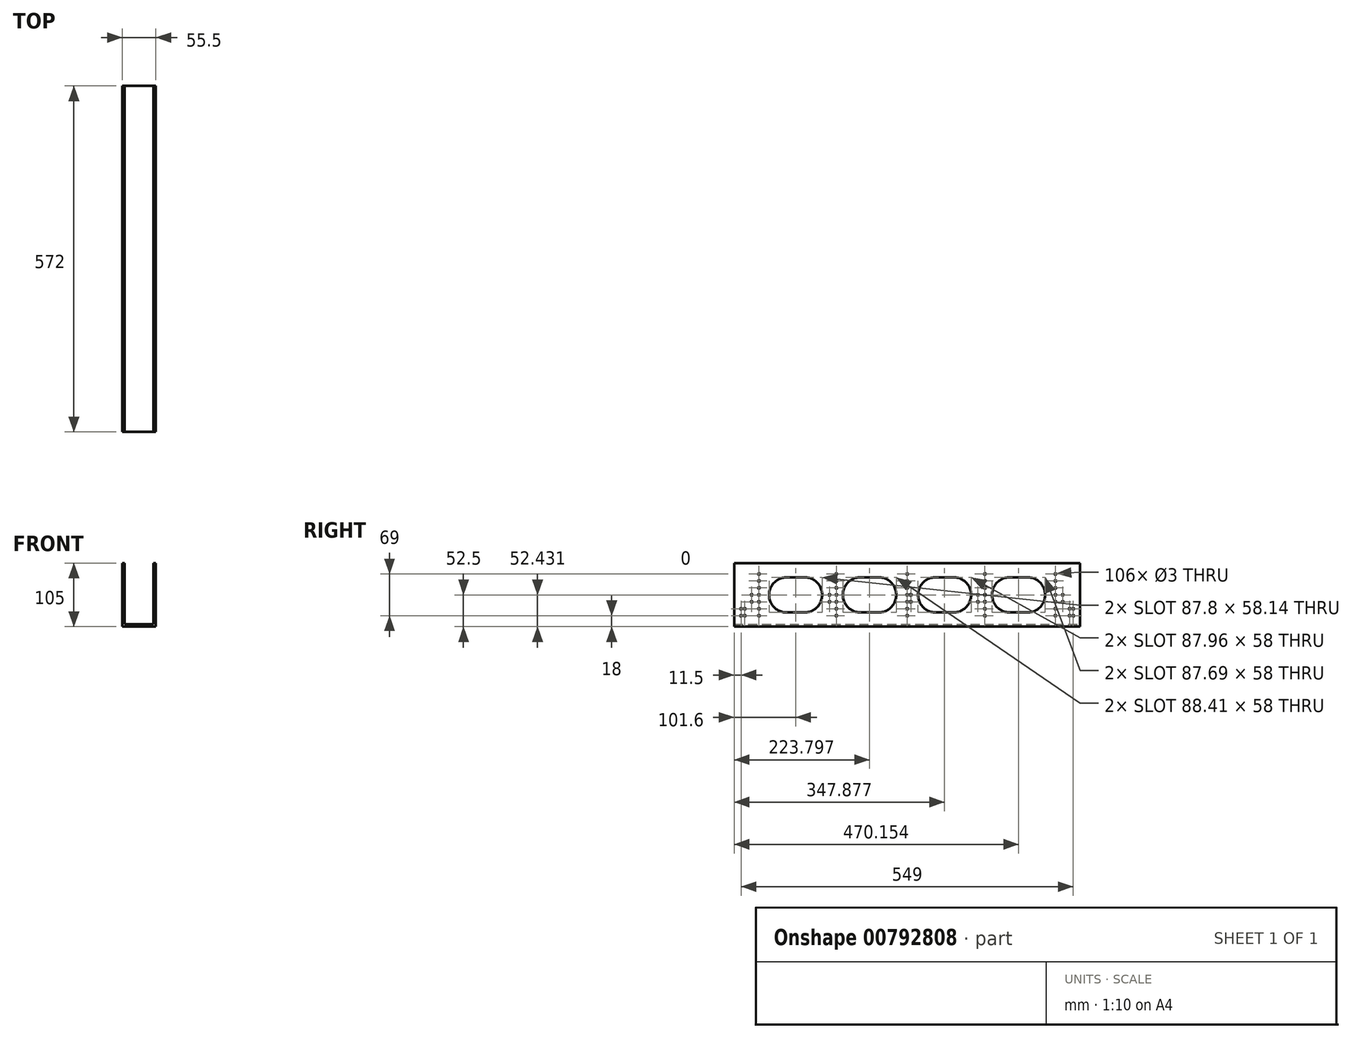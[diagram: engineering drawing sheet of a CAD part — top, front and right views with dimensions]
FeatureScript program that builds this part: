
annotation { "Feature Type Name" : "Feature", "Feature Type Description" : "" }
export const myFeature = defineFeature(function(context is Context, id is Id, definition is map)
    precondition{}
    {
        {
            var Q0;
            Q0=qCreatedBy(makeId("Right.planeOp"),FACE);
            var sketch = newSketch(context, id + "F0", { "sketchPlane" : qUnion([Q0])});
            skLineSegment(sketch, "E0.bottom", {"start": v(286, -52.5) * mm, "end": v(-286, -52.5) * mm});
            skLineSegment(sketch, "E0.top", {"start": v(286, 52.5) * mm, "end": v(-286, 52.5) * mm});
            skLineSegment(sketch, "E0.left", {"start": v(286, -52.5) * mm, "end": v(286, 52.5) * mm});
            skLineSegment(sketch, "E0.right", {"start": v(-286, -52.5) * mm, "end": v(-286, 52.5) * mm});
            skPoint(sketch, "E0.middle", {"position": v(0, 0) * mm});
            skPoint(sketch, "E1.startSnap0", {"position": v(-286, 0) * mm});
            skCircle(sketch, "E2", {"center": v(-199.3, -0.15) * mm, "radius": 29 * mm});
            skLineSegment(sketch, "E3", {"start": v(-369.82, 0) * mm, "end": v(342.23, 0) * mm, "construction": true});
            skLineSegment(sketch, "E4", {"start": v(-286, -127.41) * mm, "end": v(-286, 126.22) * mm, "construction": true});
            skCircle(sketch, "E5", {"center": v(-169.5, 0) * mm, "radius": 29 * mm});
            skCircle(sketch, "E6", {"center": v(-77.4, 0) * mm, "radius": 29 * mm});
            skCircle(sketch, "E7", {"center": v(-47, 0) * mm, "radius": 29 * mm});
            skCircle(sketch, "E8", {"center": v(46.9, 0) * mm, "radius": 29 * mm});
            skCircle(sketch, "E9", {"center": v(76.86, 0) * mm, "radius": 29 * mm});
            skCircle(sketch, "E10", {"center": v(199, 0) * mm, "radius": 29 * mm});
            skCircle(sketch, "E11", {"center": v(169.3, 0) * mm, "radius": 29 * mm});
            skLineSegment(sketch, "E12", {"start": v(-198.35, 28.83) * mm, "end": v(-169.67, 29) * mm});
            skLineSegment(sketch, "E13", {"start": v(-47.17, 29) * mm, "end": v(-77.4, 29) * mm});
            skLineSegment(sketch, "E14", {"start": v(46.72, 29) * mm, "end": v(76.86, 29) * mm});
            skLineSegment(sketch, "E15", {"start": v(198.83, 29) * mm, "end": v(169.3, 29) * mm});
            skLineSegment(sketch, "E16.MirrorCS", {"start": v(-47.17, -29) * mm, "end": v(-77.4, -29) * mm});
            skLineSegment(sketch, "E17.MirrorCS", {"start": v(46.72, -29) * mm, "end": v(76.86, -29) * mm});
            skLineSegment(sketch, "E18.MirrorCS", {"start": v(198.83, -29) * mm, "end": v(169.3, -29) * mm});
            skLineSegment(sketch, "E19", {"start": v(-198.35, -29.14) * mm, "end": v(-169.36, -29) * mm});
            skLineSegment(sketch, "E20", {"start": v(-245, 57.77) * mm, "end": v(-245, -66.65) * mm, "construction": true});
            skLineSegment(sketch, "E21", {"start": v(-257, 58.1) * mm, "end": v(-257, -66.65) * mm, "construction": true});
            skLineSegment(sketch, "E22", {"start": v(-268.5, 57.77) * mm, "end": v(-268.5, -67.94) * mm, "construction": true});
            skLineSegment(sketch, "E23", {"start": v(-274.5, -67.94) * mm, "end": v(-274.5, 57.77) * mm, "construction": true});
            skLineSegment(sketch, "E24", {"start": v(0, 76.75) * mm, "end": v(0, -90) * mm, "construction": true});
            skLineSegment(sketch, "E25", {"start": v(-117, 59.06) * mm, "end": v(-117, -74.73) * mm, "construction": true});
            skLineSegment(sketch, "E26", {"start": v(-128.5, 59.7) * mm, "end": v(-128.5, -74.73) * mm, "construction": true});
            skLineSegment(sketch, "E27", {"start": v(6, 58.74) * mm, "end": v(6, -67.94) * mm, "construction": true});
            skCircle(sketch, "E28", {"center": v(-245, 0) * mm, "radius": 1.5 * mm});
            skCircle(sketch, "E29", {"center": v(-257, 0) * mm, "radius": 1.5 * mm});
            skLineSegment(sketch, "E30.MirrorCS", {"start": v(117, 59.06) * mm, "end": v(117, -74.73) * mm, "construction": true});
            skLineSegment(sketch, "E31.MirrorCS", {"start": v(128.5, 59.7) * mm, "end": v(128.5, -74.73) * mm, "construction": true});
            skLineSegment(sketch, "E32.MirrorCS", {"start": v(245, 57.77) * mm, "end": v(245, -66.65) * mm, "construction": true});
            skLineSegment(sketch, "E33.MirrorCS", {"start": v(257, 58.1) * mm, "end": v(257, -66.65) * mm, "construction": true});
            skLineSegment(sketch, "E34.MirrorCS", {"start": v(268.5, 57.77) * mm, "end": v(268.5, -67.94) * mm, "construction": true});
            skLineSegment(sketch, "E35.MirrorCS", {"start": v(274.5, -67.94) * mm, "end": v(274.5, 57.77) * mm, "construction": true});
            skLineSegment(sketch, "E36", {"start": v(-296.34, 34.5) * mm, "end": v(18.42, 34.5) * mm, "construction": true});
            skLineSegment(sketch, "E37", {"start": v(18.42, -34.5) * mm, "end": v(-296.34, -34.5) * mm, "construction": true});
            skLineSegment(sketch, "E38", {"start": v(-296.34, 23) * mm, "end": v(18.42, 23) * mm, "construction": true});
            skLineSegment(sketch, "E39.MirrorCS", {"start": v(-296.34, -23) * mm, "end": v(18.42, -23) * mm, "construction": true});
            skCircle(sketch, "E40", {"center": v(-245, 34.5) * mm, "radius": 1.5 * mm});
            skCircle(sketch, "E41", {"center": v(-245, 23) * mm, "radius": 1.5 * mm});
            skCircle(sketch, "E42", {"center": v(-245, 11.5) * mm, "radius": 1.5 * mm});
            skCircle(sketch, "E43", {"center": v(-117, 34.5) * mm, "radius": 1.5 * mm});
            skCircle(sketch, "E44", {"center": v(-117, 23) * mm, "radius": 1.5 * mm});
            skCircle(sketch, "E45", {"center": v(-117, 11.5) * mm, "radius": 1.5 * mm});
            skCircle(sketch, "E46", {"center": v(-117, 0) * mm, "radius": 1.5 * mm});
            skCircle(sketch, "E47", {"center": v(-128.5, 0) * mm, "radius": 1.5 * mm});
            skCircle(sketch, "E48", {"center": v(-268.5, -34.5) * mm, "radius": 1.5 * mm});
            skCircle(sketch, "E49", {"center": v(-268.5, -23) * mm, "radius": 1.5 * mm});
            skCircle(sketch, "E50", {"center": v(-274.5, -34.5) * mm, "radius": 1.5 * mm});
            skCircle(sketch, "E51", {"center": v(-274.5, -23) * mm, "radius": 1.5 * mm});
            skCircle(sketch, "E52", {"center": v(-245, -11.5) * mm, "radius": 1.5 * mm});
            skCircle(sketch, "E53", {"center": v(-245, -23) * mm, "radius": 1.5 * mm});
            skCircle(sketch, "E54", {"center": v(-245, -34.5) * mm, "radius": 1.5 * mm});
            skCircle(sketch, "E55", {"center": v(-257, -11.5) * mm, "radius": 1.5 * mm});
            skCircle(sketch, "E56", {"center": v(-117, -11.5) * mm, "radius": 1.5 * mm});
            skCircle(sketch, "E57", {"center": v(-117, -23) * mm, "radius": 1.5 * mm});
            skCircle(sketch, "E58", {"center": v(-117, -34.5) * mm, "radius": 1.5 * mm});
            skCircle(sketch, "E59", {"center": v(-128.5, -11.5) * mm, "radius": 1.5 * mm});
            skCircle(sketch, "E60", {"center": v(0, 0) * mm, "radius": 1.5 * mm});
            skCircle(sketch, "E61", {"center": v(6, 0) * mm, "radius": 1.5 * mm});
            skCircle(sketch, "E62", {"center": v(0, 11.5) * mm, "radius": 1.5 * mm});
            skCircle(sketch, "E63", {"center": v(0, 23) * mm, "radius": 1.5 * mm});
            skCircle(sketch, "E64", {"center": v(0, 34.5) * mm, "radius": 1.5 * mm});
            skCircle(sketch, "E65", {"center": v(0, -11.5) * mm, "radius": 1.5 * mm});
            skCircle(sketch, "E66", {"center": v(0, -23) * mm, "radius": 1.5 * mm});
            skCircle(sketch, "E67", {"center": v(0, -34.5) * mm, "radius": 1.5 * mm});
            skCircle(sketch, "E68", {"center": v(6, -11.5) * mm, "radius": 1.5 * mm});
            skLineSegment(sketch, "E69", {"start": v(18.42, 34.5) * mm, "end": v(144.87, 34.5) * mm, "construction": true});
            skLineSegment(sketch, "E70", {"start": v(18.42, 23) * mm, "end": v(144.87, 23) * mm, "construction": true});
            skLineSegment(sketch, "E71", {"start": v(18.42, 11.5) * mm, "end": v(144.87, 11.5) * mm, "construction": true});
            skLineSegment(sketch, "E72.MirrorCS", {"start": v(18.42, -11.5) * mm, "end": v(144.87, -11.5) * mm, "construction": true});
            skLineSegment(sketch, "E73.MirrorCS", {"start": v(18.42, -23) * mm, "end": v(144.87, -23) * mm, "construction": true});
            skLineSegment(sketch, "E74.MirrorCS", {"start": v(18.42, -34.5) * mm, "end": v(144.87, -34.5) * mm, "construction": true});
            skCircle(sketch, "E75", {"center": v(128.5, 34.5) * mm, "radius": 1.5 * mm});
            skCircle(sketch, "E76", {"center": v(128.5, 23) * mm, "radius": 1.5 * mm});
            skCircle(sketch, "E77", {"center": v(128.5, 11.5) * mm, "radius": 1.5 * mm});
            skCircle(sketch, "E78", {"center": v(128.5, 0) * mm, "radius": 1.5 * mm});
            skCircle(sketch, "E79", {"center": v(128.5, -11.5) * mm, "radius": 1.5 * mm});
            skCircle(sketch, "E80", {"center": v(128.5, -23) * mm, "radius": 1.5 * mm});
            skCircle(sketch, "E81", {"center": v(128.5, -34.5) * mm, "radius": 1.5 * mm});
            skCircle(sketch, "E82", {"center": v(117, 0) * mm, "radius": 1.5 * mm});
            skCircle(sketch, "E83", {"center": v(117, -11.5) * mm, "radius": 1.5 * mm});
            skLineSegment(sketch, "E84", {"start": v(144.87, -34.5) * mm, "end": v(291.12, -34.5) * mm, "construction": true});
            skLineSegment(sketch, "E85", {"start": v(144.87, -23) * mm, "end": v(291.12, -23) * mm, "construction": true});
            skLineSegment(sketch, "E86", {"start": v(144.87, -11.5) * mm, "end": v(291.12, -11.5) * mm, "construction": true});
            skLineSegment(sketch, "E87.MirrorCS", {"start": v(144.87, 11.5) * mm, "end": v(291.12, 11.5) * mm, "construction": true});
            skLineSegment(sketch, "E88.MirrorCS", {"start": v(144.87, 23) * mm, "end": v(291.12, 23) * mm, "construction": true});
            skLineSegment(sketch, "E89.MirrorCS", {"start": v(144.87, 34.5) * mm, "end": v(291.12, 34.5) * mm, "construction": true});
            skCircle(sketch, "E90", {"center": v(245, 34.5) * mm, "radius": 1.5 * mm});
            skCircle(sketch, "E91", {"center": v(245, 23) * mm, "radius": 1.5 * mm});
            skCircle(sketch, "E92", {"center": v(245, 11.5) * mm, "radius": 1.5 * mm});
            skCircle(sketch, "E93", {"center": v(245, 0) * mm, "radius": 1.5 * mm});
            skCircle(sketch, "E94", {"center": v(245, -11.5) * mm, "radius": 1.5 * mm});
            skCircle(sketch, "E95", {"center": v(245, -23) * mm, "radius": 1.5 * mm});
            skCircle(sketch, "E96", {"center": v(245, -34.5) * mm, "radius": 1.5 * mm});
            skCircle(sketch, "E97", {"center": v(257, 0) * mm, "radius": 1.5 * mm});
            skCircle(sketch, "E98", {"center": v(257, -11.5) * mm, "radius": 1.5 * mm});
            skCircle(sketch, "E99", {"center": v(268.5, -23) * mm, "radius": 1.5 * mm});
            skCircle(sketch, "E100", {"center": v(268.5, -34.5) * mm, "radius": 1.5 * mm});
            skCircle(sketch, "E101", {"center": v(274.5, -23) * mm, "radius": 1.5 * mm});
            skCircle(sketch, "E102", {"center": v(274.5, -34.5) * mm, "radius": 1.5 * mm});
            skSolve(sketch);
        }
        {
            var Q0;
            Q0=makeQuery(id+"F0.imprint","IMPRINT",FACE,{"disambiguationData":[TD([[makeQuery(id+"F0.imprint","IMPRINT",EDGE,{"derivedFrom":sQuery(id+"F0.wireOp",EDGE,"E0.bottom")}),-1.0]])]});
            extrude(context, id + "F1", {"entities" : qUnion([Q0]), "oppositeDirection" : true, "depth" : 55.5 * mm, "offsetDistance" : 25 * mm});
        }
        {
            var Q0;
            Q0=makeQuery(id+"F1.opExtrude","SWEPT_FACE",FACE,{"disambiguationData":[OSD([sQuery(id+"F0.wireOp",EDGE,"E0.left")])]});
            var sketch = newSketch(context, id + "F2", { "sketchPlane" : qUnion([Q0])});
            skLineSegment(sketch, "E103", {"start": v(4, 52.5) * mm, "end": v(4, -48.5) * mm});
            skLineSegment(sketch, "E104", {"start": v(4, -48.5) * mm, "end": v(51.5, -48.5) * mm});
            skLineSegment(sketch, "E105", {"start": v(51.5, -48.5) * mm, "end": v(51.5, 52.5) * mm});
            skLineSegment(sketch, "E106", {"start": v(51.5, 52.5) * mm, "end": v(4, 52.5) * mm});
            skSolve(sketch);
        }
        {
            var Q0;
            Q0 = qSketchRegion(id + "F2", true);
            extrude(context, id + "F3", {"entities" : qUnion([Q0]), "operationType" : NewBodyOperationType.REMOVE, "oppositeDirection" : true, "depth" : 577 * mm, "offsetDistance" : 25 * mm});
        }
    });
